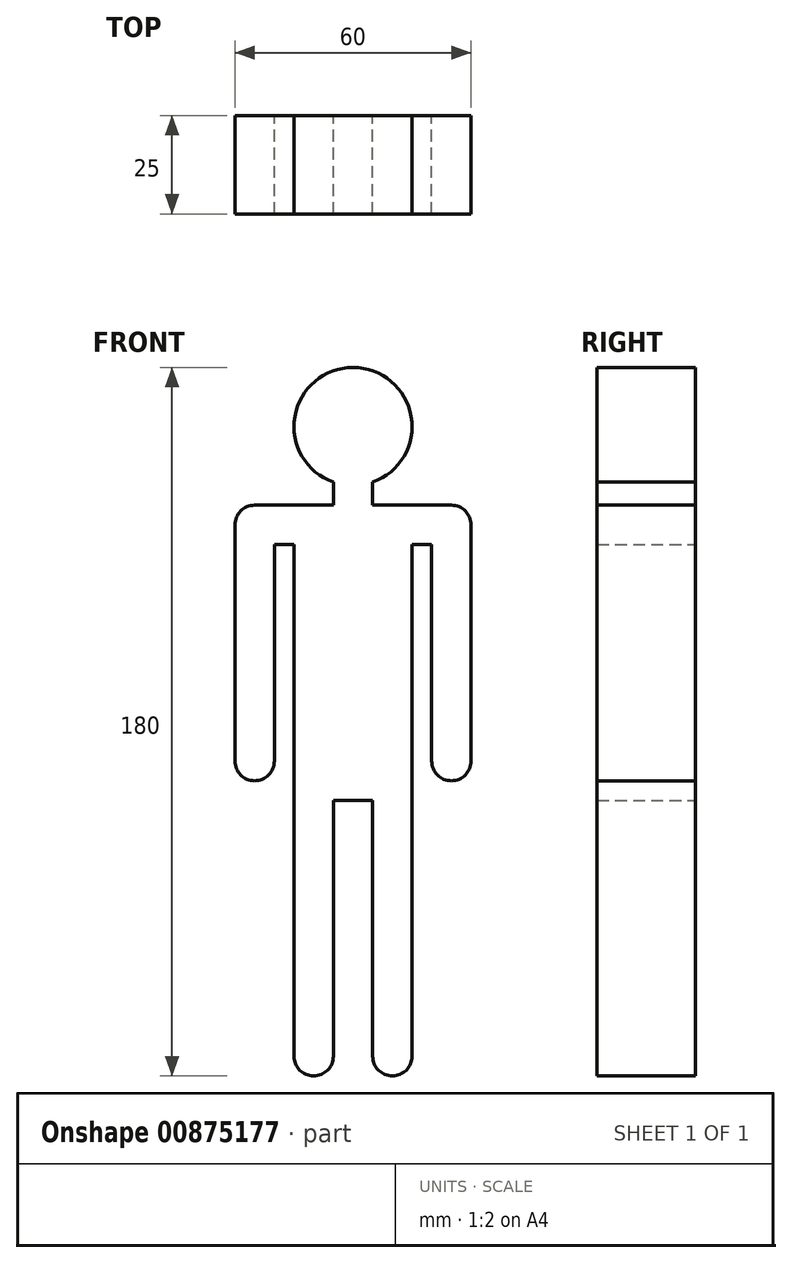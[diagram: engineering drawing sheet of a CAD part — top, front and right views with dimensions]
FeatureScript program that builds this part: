
annotation { "Feature Type Name" : "Feature", "Feature Type Description" : "" }
export const myFeature = defineFeature(function(context is Context, id is Id, definition is map)
    precondition{}
    {
        {
            var Q0;
            Q0=qCreatedBy(makeId("Front.planeOp"),FACE);
            var sketch = newSketch(context, id + "F0", { "sketchPlane" : qUnion([Q0])});
            skLineSegment(sketch, "E0.top", {"start": v(0, 180) * mm, "end": v(60, 180) * mm, "construction": true});
            skLineSegment(sketch, "E0.left", {"start": v(0, 0) * mm, "end": v(0, 180) * mm, "construction": true});
            skLineSegment(sketch, "E0.right", {"start": v(60, 0) * mm, "end": v(60, 180) * mm, "construction": true});
            skCircle(sketch, "E1", {"center": v(30, 165) * mm, "radius": 15 * mm});
            skPoint(sketch, "E1.centerSnap0", {"position": v(30, 180) * mm});
            skLineSegment(sketch, "E2", {"start": v(30, 165) * mm, "end": v(30, 140) * mm});
            skLineSegment(sketch, "E3", {"start": v(30, 140) * mm, "end": v(5, 140) * mm});
            skLineSegment(sketch, "E4", {"start": v(5, 140) * mm, "end": v(5, 80) * mm});
            skLineSegment(sketch, "E5", {"start": v(30, 140) * mm, "end": v(55, 140) * mm});
            skLineSegment(sketch, "E6", {"start": v(55, 140) * mm, "end": v(55, 80) * mm});
            skLineSegment(sketch, "E7", {"start": v(30, 140) * mm, "end": v(30, 75) * mm});
            skLineSegment(sketch, "E8", {"start": v(30, 75) * mm, "end": v(20, 75) * mm});
            skLineSegment(sketch, "E9", {"start": v(20, 75) * mm, "end": v(30, 75) * mm});
            skLineSegment(sketch, "E10", {"start": v(30, 75) * mm, "end": v(40, 75) * mm});
            skLineSegment(sketch, "E11", {"start": v(20, 75) * mm, "end": v(20, 5) * mm});
            skLineSegment(sketch, "E12", {"start": v(40, 75) * mm, "end": v(40, 5) * mm});
            skArc(sketch, "E13.0.startCap", {"start": v(0, 140) * mm, "mid": v(5, 145) * mm, "end": v(10, 140) * mm});
            skArc(sketch, "E13.0.endCap", {"start": v(10, 80) * mm, "mid": v(5, 75) * mm, "end": v(0, 80) * mm});
            skLineSegment(sketch, "E13.0.left", {"start": v(10, 140) * mm, "end": v(10, 80) * mm});
            skLineSegment(sketch, "E13.0.right", {"start": v(0, 140) * mm, "end": v(0, 80) * mm});
            skArc(sketch, "E13.1.startCap", {"start": v(30, 145) * mm, "mid": v(35, 140) * mm, "end": v(30, 135) * mm});
            skArc(sketch, "E13.1.endCap", {"start": v(5, 135) * mm, "mid": v(0, 140) * mm, "end": v(5, 145) * mm});
            skLineSegment(sketch, "E13.1.left", {"start": v(30, 135) * mm, "end": v(5, 135) * mm});
            skLineSegment(sketch, "E13.1.right", {"start": v(30, 145) * mm, "end": v(5, 145) * mm});
            skArc(sketch, "E13.2.startCap", {"start": v(30, 135) * mm, "mid": v(25, 140) * mm, "end": v(30, 145) * mm});
            skArc(sketch, "E13.2.endCap", {"start": v(55, 145) * mm, "mid": v(60, 140) * mm, "end": v(55, 135) * mm});
            skLineSegment(sketch, "E13.2.left", {"start": v(30, 145) * mm, "end": v(55, 145) * mm});
            skLineSegment(sketch, "E13.2.right", {"start": v(30, 135) * mm, "end": v(55, 135) * mm});
            skArc(sketch, "E13.3.startCap", {"start": v(50, 140) * mm, "mid": v(55, 145) * mm, "end": v(60, 140) * mm});
            skArc(sketch, "E13.3.endCap", {"start": v(60, 80) * mm, "mid": v(55, 75) * mm, "end": v(50, 80) * mm});
            skLineSegment(sketch, "E13.3.left", {"start": v(60, 140) * mm, "end": v(60, 80) * mm});
            skLineSegment(sketch, "E13.3.right", {"start": v(50, 140) * mm, "end": v(50, 80) * mm});
            skArc(sketch, "E13.4.startCap", {"start": v(35, 75) * mm, "mid": v(40, 80) * mm, "end": v(45, 75) * mm});
            skArc(sketch, "E13.4.endCap", {"start": v(45, 5) * mm, "mid": v(40, 0) * mm, "end": v(35, 5) * mm});
            skLineSegment(sketch, "E13.4.left", {"start": v(45, 75) * mm, "end": v(45, 5) * mm});
            skLineSegment(sketch, "E13.4.right", {"start": v(35, 75) * mm, "end": v(35, 5) * mm});
            skArc(sketch, "E13.5.startCap", {"start": v(15, 75) * mm, "mid": v(20, 80) * mm, "end": v(25, 75) * mm});
            skArc(sketch, "E13.5.endCap", {"start": v(25, 5) * mm, "mid": v(20, 0) * mm, "end": v(15, 5) * mm});
            skLineSegment(sketch, "E13.5.left", {"start": v(25, 75) * mm, "end": v(25, 5) * mm});
            skLineSegment(sketch, "E13.5.right", {"start": v(15, 75) * mm, "end": v(15, 5) * mm});
            skLineSegment(sketch, "E14", {"start": v(0, 0) * mm, "end": v(60, 0) * mm, "construction": true});
            skLineSegment(sketch, "E15", {"start": v(15, 75) * mm, "end": v(15, 135) * mm});
            skLineSegment(sketch, "E16", {"start": v(45, 75) * mm, "end": v(45, 135) * mm});
            skLineSegment(sketch, "E17", {"start": v(25, 70) * mm, "end": v(30, 70) * mm});
            skLineSegment(sketch, "E18", {"start": v(30, 75) * mm, "end": v(30, 70) * mm, "construction": true});
            skLineSegment(sketch, "E19", {"start": v(30, 70) * mm, "end": v(35, 70) * mm});
            skLineSegment(sketch, "E20", {"start": v(30, 150) * mm, "end": v(30, 145) * mm, "construction": true});
            skLineSegment(sketch, "E21", {"start": v(25, 140) * mm, "end": v(25, 150.86) * mm});
            skLineSegment(sketch, "E22", {"start": v(35, 140) * mm, "end": v(35, 150.86) * mm});
            skLineSegment(sketch, "E23", {"start": v(5, 140) * mm, "end": v(-55, 140) * mm, "construction": true});
            skLineSegment(sketch, "E24", {"start": v(55, 140) * mm, "end": v(115, 140) * mm, "construction": true});
            skLineSegment(sketch, "E25", {"start": v(5, 140) * mm, "end": v(5, 145) * mm, "construction": true});
            skCircle(sketch, "E26", {"center": v(-55, 140) * mm, "radius": 5 * mm, "construction": true});
            skCircle(sketch, "E27", {"center": v(115, 140) * mm, "radius": 5 * mm, "construction": true});
            skSolve(sketch);
        }
        {
            var Q0;
            Q0=qSketchRegion(id+"F0",true);
            var Q1;
            {var subQ0=sQuery(id+"F0.wireOp",EDGE,"E5");var subQ3=sQuery(id+"F0.wireOp",EDGE,"E13.1.startCap");var subQ5=makeQuery(id+"F0.imprint","INTERSECT",VERTEX,{"derivedFrom":[subQ0,subQ3,sQuery(id+"F0.wireOp",EDGE,"E22")]});Q1=makeQuery(id+"F0.imprint","IMPRINT",FACE,{"disambiguationData":[TD([[makeQuery(id+"F0.imprint","IMPRINT",EDGE,{"disambiguationData":[TD([[subQ5,1.0]])],"derivedFrom":subQ0}),1.0]])]});}
            var Q2;
            {var subQ0=sQuery(id+"F0.wireOp",EDGE,"E3");var subQ3=sQuery(id+"F0.wireOp",EDGE,"E13.2.startCap");var subQ5=makeQuery(id+"F0.imprint","INTERSECT",VERTEX,{"derivedFrom":[subQ0,subQ3,sQuery(id+"F0.wireOp",EDGE,"E21")]});Q2=makeQuery(id+"F0.imprint","IMPRINT",FACE,{"disambiguationData":[TD([[makeQuery(id+"F0.imprint","IMPRINT",EDGE,{"disambiguationData":[TD([[subQ5,1.0]])],"derivedFrom":subQ0}),-1.0]])]});}
            var Q3;
            {var subQ1=sQuery(id+"F0.wireOp",EDGE,"E3");var subQ3=sQuery(id+"F0.wireOp",EDGE,"E13.2.startCap");var subQ4=makeQuery(id+"F0.imprint","INTERSECT",VERTEX,{"derivedFrom":[subQ1,subQ3,sQuery(id+"F0.wireOp",EDGE,"E21")]});Q3=makeQuery(id+"F0.imprint","IMPRINT",FACE,{"disambiguationData":[TD([[makeQuery(id+"F0.imprint","IMPRINT",EDGE,{"disambiguationData":[TD([[subQ4,1.0]])],"derivedFrom":subQ1}),1.0]])]});}
            var Q4;
            {var subQ1=sQuery(id+"F0.wireOp",EDGE,"E5");var subQ3=sQuery(id+"F0.wireOp",EDGE,"E13.1.startCap");var subQ4=makeQuery(id+"F0.imprint","INTERSECT",VERTEX,{"derivedFrom":[subQ1,subQ3,sQuery(id+"F0.wireOp",EDGE,"E22")]});Q4=makeQuery(id+"F0.imprint","IMPRINT",FACE,{"disambiguationData":[TD([[makeQuery(id+"F0.imprint","IMPRINT",EDGE,{"disambiguationData":[TD([[subQ4,1.0]])],"derivedFrom":subQ1}),-1.0]])]});}
            extrude(context, id + "F1", {"entities" : qUnion([Q0, Q1, Q2, Q3, Q4]), "depth" : 25 * mm, "offsetDistance" : 25 * mm});
        }
    });
